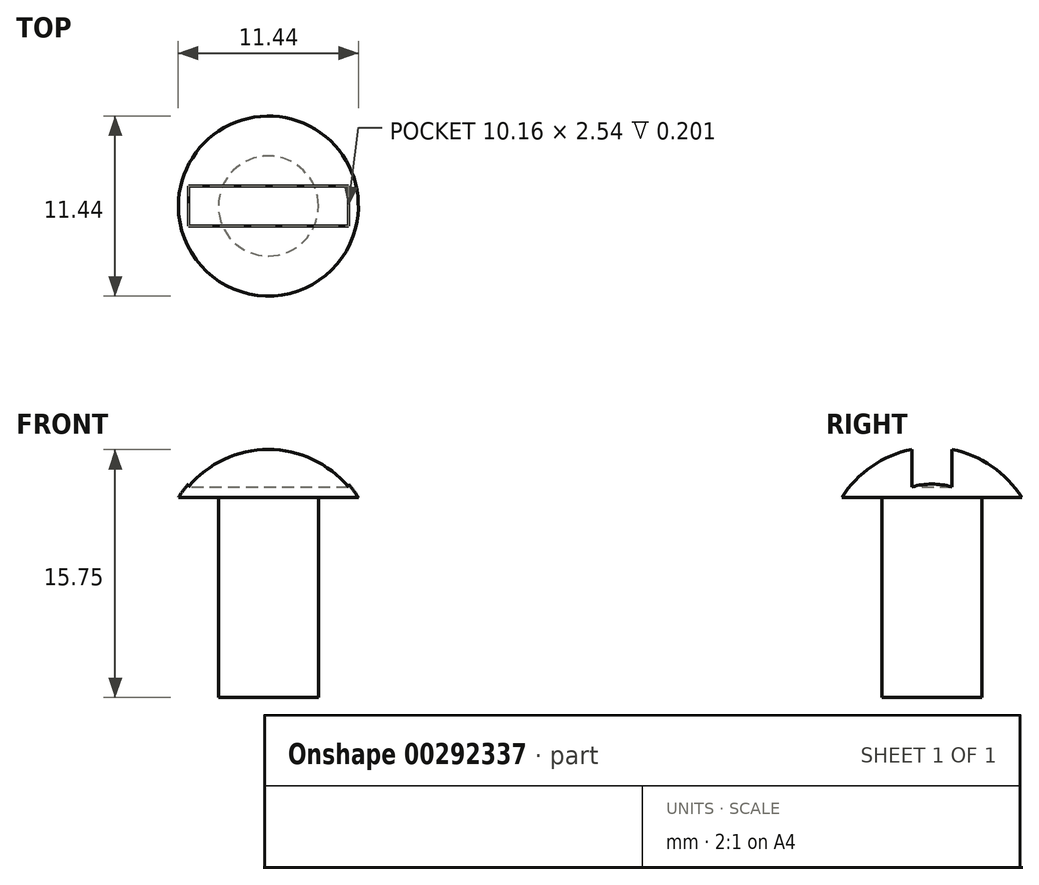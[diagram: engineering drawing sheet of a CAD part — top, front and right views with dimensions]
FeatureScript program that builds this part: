
annotation { "Feature Type Name" : "Feature", "Feature Type Description" : "" }
export const myFeature = defineFeature(function(context is Context, id is Id, definition is map)
    precondition{}
    {
        {
            var Q0;
            Q0=qCreatedBy(makeId("Front.planeOp"),FACE);
            var sketch = newSketch(context, id + "F0", { "sketchPlane" : qUnion([Q0])});
            skLineSegment(sketch, "E0.bottom", {"start": v(0, 0) * mm, "end": v(3.17, 0) * mm});
            skLineSegment(sketch, "E0.left", {"start": v(0, 0) * mm, "end": v(0, 12.7) * mm});
            skLineSegment(sketch, "E0.right", {"start": v(3.18, 0) * mm, "end": v(3.17, 12.7) * mm});
            skLineSegment(sketch, "E1", {"start": v(3.17, 12.7) * mm, "end": v(5.71, 12.7) * mm});
            skLineSegment(sketch, "E2", {"start": v(0, 12.7) * mm, "end": v(0, 15.88) * mm});
            skArc(sketch, "E3", {"start": v(5.71, 12.7) * mm, "mid": v(3.27, 15.03) * mm, "end": v(0, 15.88) * mm});
            skSolve(sketch);
        }
        {
            var Q0;
            Q0=makeQuery(id+"F0.imprint","IMPRINT",FACE,{"disambiguationData":[TD([[makeQuery(id+"F0.imprint","IMPRINT",EDGE,{"derivedFrom":sQuery(id+"F0.wireOp",EDGE,"E0.bottom")}),1.0]])]});
            var Q1;
            Q1=sQuery(id+"F0.wireOp",EDGE,"E0.left");
            revolve(context, id + "F1", {"entities" : qUnion([Q0]), "axis" : qUnion([Q1]), "revolveType" : RevolveType.FULL});
        }
        {
            var Q0;
            Q0=qCreatedBy(makeId("Right.planeOp"),FACE);
            var sketch = newSketch(context, id + "F2", { "sketchPlane" : qUnion([Q0])});
            skLineSegment(sketch, "E4.bottom", {"start": v(1.27, 15.9) * mm, "end": v(-1.27, 15.9) * mm});
            skLineSegment(sketch, "E4.top", {"start": v(1.27, 13.36) * mm, "end": v(-1.27, 13.36) * mm});
            skLineSegment(sketch, "E4.left", {"start": v(1.27, 15.9) * mm, "end": v(1.27, 13.36) * mm});
            skLineSegment(sketch, "E4.right", {"start": v(-1.27, 15.9) * mm, "end": v(-1.27, 13.36) * mm});
            skPoint(sketch, "E4.middle", {"position": v(0, 14.63) * mm});
            skSolve(sketch);
        }
        {
            var Q0;
            Q0 = qSketchRegion(id + "F2", true);
            extrude(context, id + "F3", {"entities" : qUnion([Q0]), "operationType" : NewBodyOperationType.REMOVE, "endBound" : BoundingType.SYMMETRIC, "depth" : 10.16 * mm});
        }
    });
